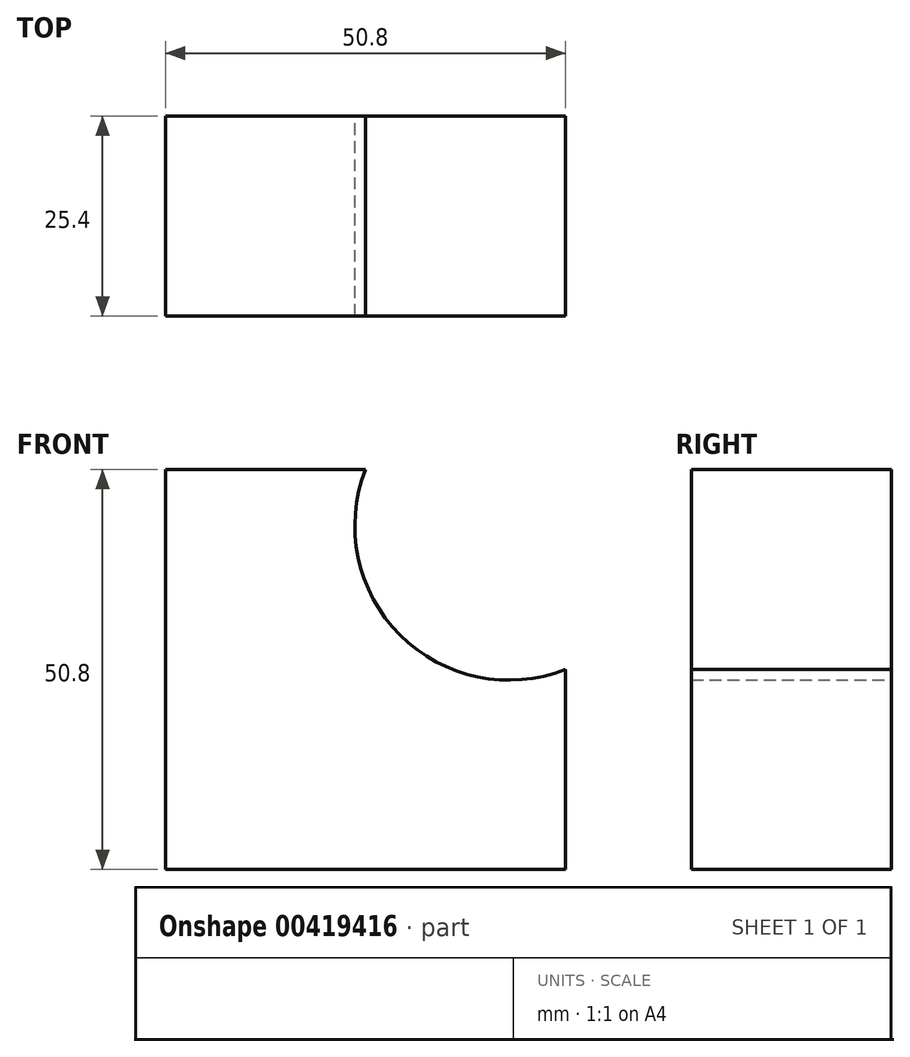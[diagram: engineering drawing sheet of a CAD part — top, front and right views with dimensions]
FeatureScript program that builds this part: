
annotation { "Feature Type Name" : "Feature", "Feature Type Description" : "" }
export const myFeature = defineFeature(function(context is Context, id is Id, definition is map)
    precondition{}
    {
        {
            var Q0;
            Q0=qCreatedBy(makeId("Front.planeOp"),FACE);
            var sketch = newSketch(context, id + "F0", { "sketchPlane" : qUnion([Q0])});
            skLineSegment(sketch, "E0", {"start": v(-54.8, 40.49) * mm, "end": v(-54.8, -10.31) * mm});
            skLineSegment(sketch, "E1", {"start": v(-54.8, 40.49) * mm, "end": v(-29.4, 40.49) * mm});
            skLineSegment(sketch, "E2", {"start": v(-54.8, -10.31) * mm, "end": v(-4, -10.31) * mm});
            skLineSegment(sketch, "E3", {"start": v(-4, -10.31) * mm, "end": v(-4, 15.09) * mm});
            skArc(sketch, "E4", {"start": v(-29.4, 40.49) * mm, "mid": v(-25.02, 19.48) * mm, "end": v(-4, 15.09) * mm});
            skSolve(sketch);
        }
        {
            var Q0;
            Q0 = qSketchRegion(id + "F0", true);
            extrude(context, id + "F1", {"entities" : qUnion([Q0]), "depth" : 25.4 * mm});
        }
    });
